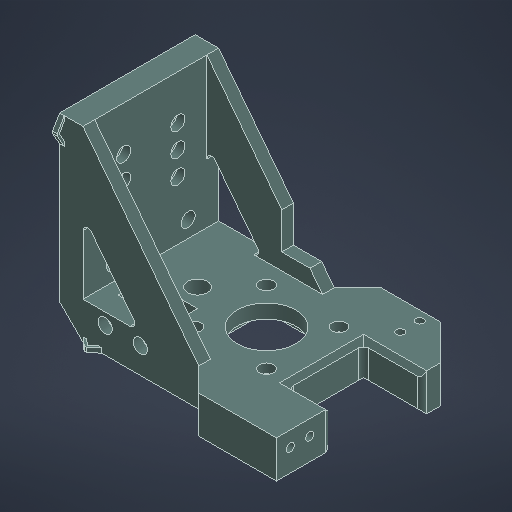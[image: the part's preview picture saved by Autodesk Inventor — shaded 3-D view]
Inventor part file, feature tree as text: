
AUTODESK INVENTOR PART (.ipt)
format: ipt  version: 2025.1 (Build 291241000, 241)  size: 992,768 bytes
history: native  units: in
note: dims shown in document units (in); Inventor stores cm internally (conversion verified against a paired STEP export)
features: extrude x17, sketch x10, chamfer x4, plane x3, fillet x2, mirror x1, projected_geometry x1
ambient origin geometry x8: Origin, YZ Plane, XZ Plane, XY Plane, X Axis, Y Axis, Z Axis, Center Point
bodies: Solid1 (feature_tree)
feature tree (38):
  sketch  "Sketch1"  dims[d0=3.0709in d1=4.3307in]
  extrude  "Extrusion1"  Depth=4.3307in
  extrude  "Extrusion21"  Depth=0.9843in
  extrude  "Extrusion2"  Depth=0.8465in
  plane  "Work Plane1"
  extrude  "Extrusion3"  Depth=1.1811in
  extrude  "Extrusion4"  Depth=0.2362in
  sketch  "Sketch3"  dims[d6=1.6929in d7=0.8465in]
  extrude  "Extrusion5"  Depth=0.2362in
  extrude  "Extrusion6"  Depth=0.2362in
  extrude  "Extrusion7"  Depth=0.1575in
  sketch  "Sketch4"  dims[d8=0.3307in d9=1.1811in]
  chamfer  "Chamfer1"  Distance=0.3937in
  sketch  "Sketch5"  dims[d11=0.1339in d12=0.2362in]
  plane  "Work Plane2"
  chamfer  "Chamfer3"  Distance=0.6299in
  fillet  "Fillet3"  Radius=3.1496in
  extrude  "Extrusion13"  [1 undecoded]
  plane  "Work Plane4"
  mirror  "Mirror2"
  extrude  "Extrusion14"  Depth=0.1575in TaperAngle=0.0deg
  extrude  "Extrusion15"  Depth=0.1575in
  chamfer  "Chamfer7"  Distance=0.2559in
  fillet  "Fillet8"  Radius=0.3268in
  extrude  "Extrusion16"  Depth=0.1575in
  extrude  "Extrusion17"  Depth=0.1575in TaperAngle=0.0deg
  sketch  "Sketch8"  dims[d17=0.1575in d18=0.3268in]
  extrude  "Extrusion18"  Depth=0.1575in
  extrude  "Extrusion19"  TaperAngle=0.0deg  [1 undecoded]
  extrude  "Extrusion20"  Depth=0.1575in
  chamfer  "Chamfer6"  Distance=0.6299in
  extrude  "Extrusion22"  Depth=0.1575in
  sketch  "Sketch2"  dims[d3=0.9843in d5=0.9843in]
  sketch  "Sketch6"  dims[d13=0.2362in d14=0.2362in]
  sketch  "Sketch7"  dims[d15=0.2362in d16=0.1339in]
  sketch  "Sketch9"  dims[d19=0.1969in]
  projected_geometry  "Projected Loop1"
  sketch  "Sketch10"  dims[d20=0.1969in d21=0.3937in d22=0.6299in d23=0.0in d24=3.1496in d25=0.0in d26=-0.3937in d27=3.5433in d28=0.0in d29=0.1339in d30=0.2559in d31=0.3268in d32=0.2333in d33=0.315in d34=0.0in d35=0.2323in d36=0.0in d37=0.2756in d38=0.6299in d39=0.9134in d41=0.3937in d42=1.7717in d43=0.3937in d44=0.3937in d45=0.2362in d46=0.8775in d47=0.0in d48=0.1378in d49=0.0in d51=0.3937in d52=3.5433in d53=0.0in d54=0.3937in d55=0.0787in d56=45.0deg d57=0.7874in d60=-1.1417in d66=0.0787in d67=0.0787in d68=45.0deg d69=0.0787in d94=0.1969in d95=0.0in d96=-1.1417in d97=0.2756in d99=0.689in d100=2.3622in d101=0.0in d102=0.1339in d103=0.1969in d105=1.0236in d106=0.315in d107=0.0in d108=0.2854in d109=1.2598in d110=2.3425in d111=0.5906in d112=0.0787in d113=45.0deg d114=0.3937in d115=0.0787in d116=45.0deg d117=0.0787in d118=0.1181in d119=0.1575in d120=0.0in d121=0.3189in d124=0.8661in d125=0.2362in d126=0.0in d127=0.0in d128=0.1181in d129=0.5906in d130=0.3937in d131=0.0in d132=0.1969in d133=30.0deg d134=0.1181in d135=0.0394in d136=0.0394in d137=0.0787in d138=0.0in d142=0.0394in d143=0.1181in d144=0.0394in d145=0.315in d146=0.0787in d147=0.0in d148=0.4724in d149=0.1575in d150=0.2362in d151=0.1575in d152=0.0in d153=0.2362in d154=0.1575in d155=0.0in]
note: 2 required parameter values undecoded (feature->parameter linkage not recoverable at this tier; creation-order binding heuristic only, values carry confidence <= 0.55)
